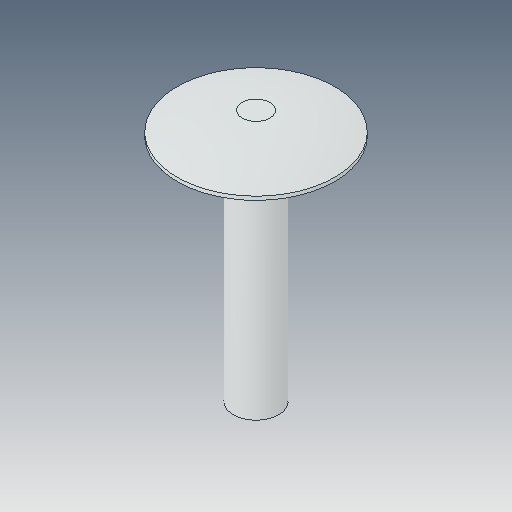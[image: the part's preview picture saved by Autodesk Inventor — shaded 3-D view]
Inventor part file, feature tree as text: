
AUTODESK INVENTOR PART (.ipt)
format: ipt  version: 2023.5 (Build 275446000, 446)  size: 99,328 bytes
history: native  units: in
note: dims shown in document units (in); Inventor stores cm internally (conversion verified against a paired STEP export)
features: revolve x1
ambient origin geometry x8: Origin, YZ Plane, XZ Plane, XY Plane, X Axis, Y Axis, Z Axis, Center Point
bodies: Solid1 (feature_tree)
feature tree (1):
  revolve  "Revolve1"  [1 undecoded]
note: 1 required parameter value undecoded (feature->parameter linkage not recoverable at this tier; creation-order binding heuristic only, values carry confidence <= 0.55)
